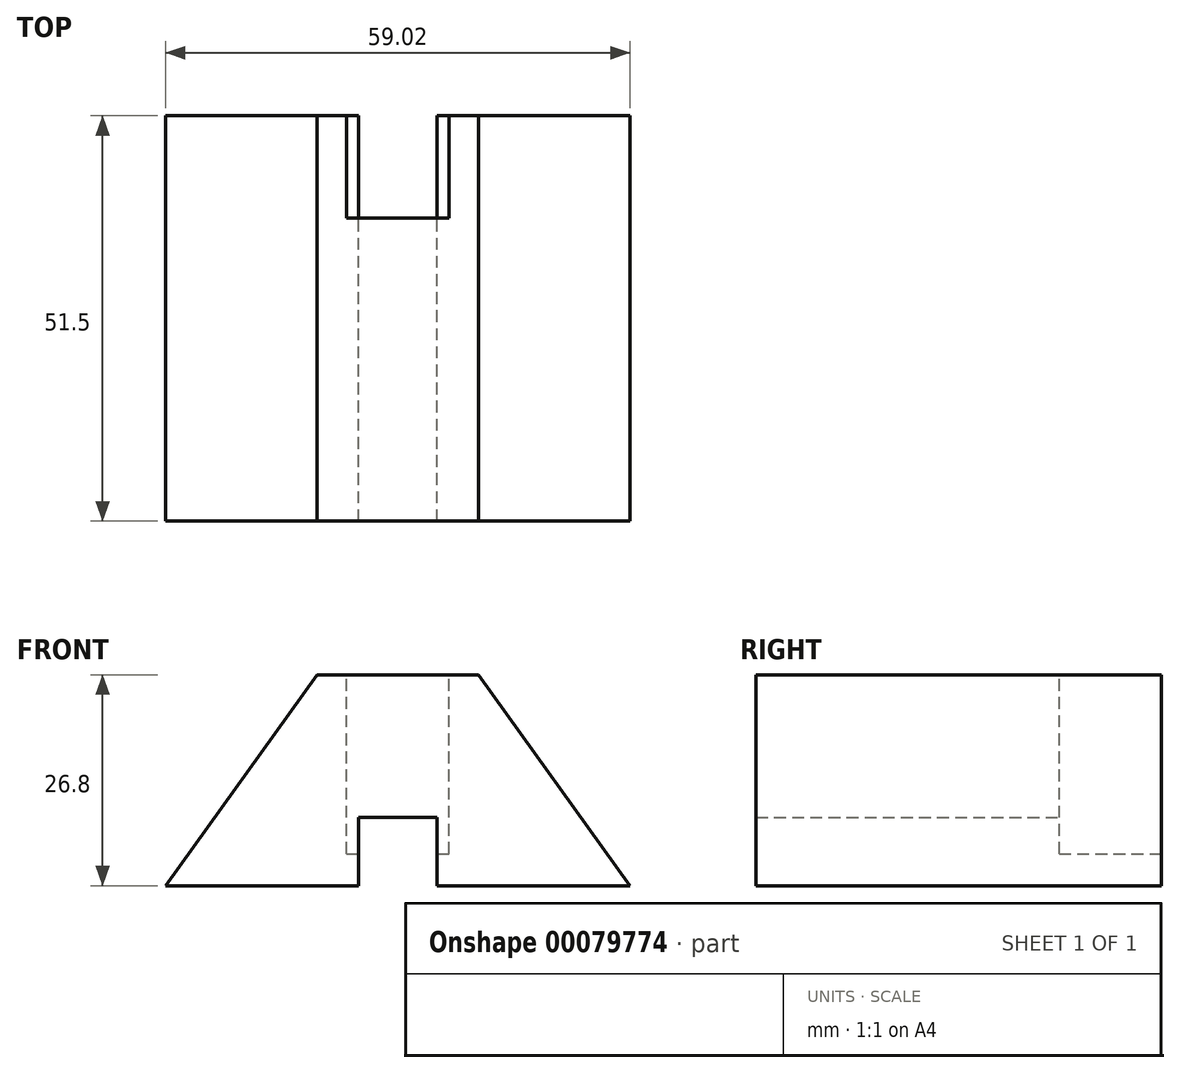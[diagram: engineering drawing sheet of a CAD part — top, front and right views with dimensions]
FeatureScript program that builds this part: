
annotation { "Feature Type Name" : "Feature", "Feature Type Description" : "" }
export const myFeature = defineFeature(function(context is Context, id is Id, definition is map)
    precondition{}
    {
        {
            var Q0;
            Q0=qCreatedBy(makeId("Front.planeOp"),FACE);
            var sketch = newSketch(context, id + "F0", { "sketchPlane" : qUnion([Q0])});
            skLineSegment(sketch, "E0", {"start": v(-29.5, 0) * mm, "end": v(29.5, 0) * mm});
            skLineSegment(sketch, "E1", {"start": v(-10.25, 26.8) * mm, "end": v(10.25, 26.8) * mm});
            skLineSegment(sketch, "E2", {"start": v(10.25, 26.8) * mm, "end": v(29.5, 0) * mm});
            skLineSegment(sketch, "E3", {"start": v(-10.25, 26.8) * mm, "end": v(-29.5, 0) * mm});
            skLineSegment(sketch, "E4.bottom", {"start": v(-5, 0) * mm, "end": v(5, 0) * mm});
            skLineSegment(sketch, "E4.top", {"start": v(-5, 8.67) * mm, "end": v(5, 8.67) * mm});
            skLineSegment(sketch, "E4.left", {"start": v(-5, 0) * mm, "end": v(-5, 8.67) * mm});
            skLineSegment(sketch, "E4.right", {"start": v(5, 0) * mm, "end": v(5, 8.67) * mm});
            skSolve(sketch);
        }
        {
            var Q0;
            Q0=makeQuery(id+"F0.imprint","IMPRINT",FACE,{"disambiguationData":[TD([[makeQuery(id+"F0.imprint","IMPRINT",EDGE,{"derivedFrom":sQuery(id+"F0.wireOp",EDGE,"E1")}),-1.0]])]});
            extrude(context, id + "F1", {"entities" : qUnion([Q0]), "depth" : 51.5 * mm});
        }
        {
            var Q0;
            Q0=makeQuery(id+"F1.opExtrude","SWEPT_FACE",FACE,{"disambiguationData":[OSD([sQuery(id+"F0.wireOp",EDGE,"E1")])]});
            var sketch = newSketch(context, id + "F2", { "sketchPlane" : qUnion([Q0])});
            skLineSegment(sketch, "E5.bottom", {"start": v(-6.5, 0) * mm, "end": v(6.5, 0) * mm});
            skLineSegment(sketch, "E5.top", {"start": v(-6.5, -13) * mm, "end": v(6.5, -13) * mm});
            skLineSegment(sketch, "E5.left", {"start": v(-6.5, 0) * mm, "end": v(-6.5, -13) * mm});
            skLineSegment(sketch, "E5.right", {"start": v(6.5, 0) * mm, "end": v(6.5, -13) * mm});
            skSolve(sketch);
        }
        {
            var Q0;
            Q0=makeQuery(id+"F2.imprint","IMPRINT",FACE,{"disambiguationData":[TD([[makeQuery(id+"F2.imprint","IMPRINT",EDGE,{"derivedFrom":sQuery(id+"F2.wireOp",EDGE,"E5.bottom")}),-1.0]])]});
            extrude(context, id + "F3", {"entities" : qUnion([Q0]), "operationType" : NewBodyOperationType.REMOVE, "oppositeDirection" : true, "depth" : 22.75 * mm});
        }
    });
